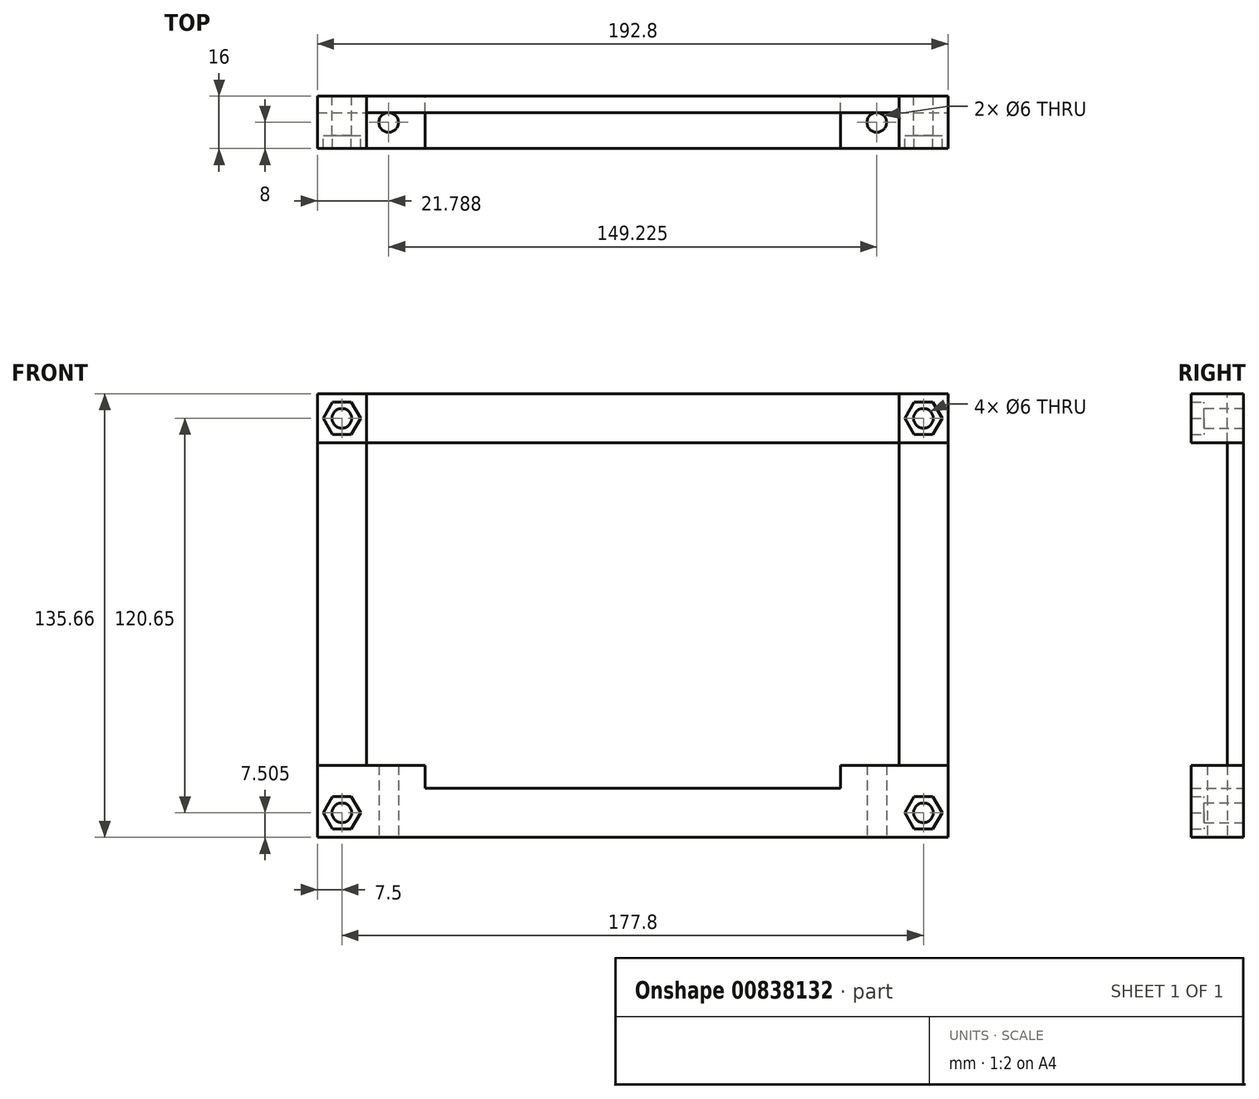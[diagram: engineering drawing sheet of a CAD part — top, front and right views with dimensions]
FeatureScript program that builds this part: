
annotation { "Feature Type Name" : "Feature", "Feature Type Description" : "" }
export const myFeature = defineFeature(function(context is Context, id is Id, definition is map)
    precondition{}
    {
        {
            var Q0;
            Q0=qCreatedBy(makeId("Front.planeOp"),FACE);
            var sketch = newSketch(context, id + "F0", { "sketchPlane" : qUnion([Q0])});
            skLineSegment(sketch, "E0.bottom", {"start": v(-88.9, 60.33) * mm, "end": v(88.9, 60.33) * mm, "construction": true});
            skLineSegment(sketch, "E0.top", {"start": v(-88.9, -60.32) * mm, "end": v(88.9, -60.32) * mm, "construction": true});
            skLineSegment(sketch, "E0.left", {"start": v(-88.9, 60.33) * mm, "end": v(-88.9, -60.32) * mm, "construction": true});
            skLineSegment(sketch, "E0.right", {"start": v(88.9, 60.33) * mm, "end": v(88.9, -60.32) * mm, "construction": true});
            skPoint(sketch, "E0.middle", {"position": v(0, 0) * mm});
            skCircle(sketch, "E1", {"center": v(-88.9, 60.33) * mm, "radius": 3 * mm});
            skCircle(sketch, "E2", {"center": v(88.9, 60.32) * mm, "radius": 3 * mm});
            skCircle(sketch, "E3", {"center": v(88.9, -60.32) * mm, "radius": 3 * mm});
            skCircle(sketch, "E4", {"center": v(-88.9, -60.32) * mm, "radius": 3 * mm});
            skLineSegment(sketch, "E5.bottom", {"start": v(-88.9, 60.33) * mm, "end": v(-96.4, 60.33) * mm, "construction": true});
            skLineSegment(sketch, "E5.top", {"start": v(-88.9, 67.83) * mm, "end": v(-96.4, 67.83) * mm, "construction": true});
            skLineSegment(sketch, "E5.left", {"start": v(-88.9, 60.33) * mm, "end": v(-88.9, 67.83) * mm, "construction": true});
            skLineSegment(sketch, "E5.right", {"start": v(-96.4, 60.33) * mm, "end": v(-96.4, 67.83) * mm, "construction": true});
            skLineSegment(sketch, "E6.bottom", {"start": v(88.9, -60.32) * mm, "end": v(96.4, -60.32) * mm, "construction": true});
            skLineSegment(sketch, "E6.top", {"start": v(88.9, -67.83) * mm, "end": v(96.4, -67.83) * mm, "construction": true});
            skLineSegment(sketch, "E6.left", {"start": v(88.9, -60.32) * mm, "end": v(88.9, -67.83) * mm, "construction": true});
            skLineSegment(sketch, "E6.right", {"start": v(96.4, -60.32) * mm, "end": v(96.4, -67.82) * mm, "construction": true});
            skLineSegment(sketch, "E7.bottom", {"start": v(-96.4, 67.83) * mm, "end": v(-81.4, 67.83) * mm});
            skLineSegment(sketch, "E7.top", {"start": v(-96.4, -67.83) * mm, "end": v(-81.4, -67.83) * mm});
            skLineSegment(sketch, "E7.left", {"start": v(-96.4, 67.83) * mm, "end": v(-96.4, -67.83) * mm});
            skLineSegment(sketch, "E7.right", {"start": v(-81.4, 67.82) * mm, "end": v(-81.4, -67.83) * mm});
            skLineSegment(sketch, "E8.bottom", {"start": v(96.4, -67.82) * mm, "end": v(-96.4, -67.83) * mm});
            skLineSegment(sketch, "E8.top", {"start": v(96.4, -52.83) * mm, "end": v(-96.4, -52.83) * mm});
            skLineSegment(sketch, "E8.left", {"start": v(96.4, -67.82) * mm, "end": v(96.4, -52.82) * mm});
            skLineSegment(sketch, "E8.right", {"start": v(-96.4, -67.83) * mm, "end": v(-96.4, -52.83) * mm});
            skLineSegment(sketch, "E9.bottom", {"start": v(96.4, -67.83) * mm, "end": v(81.4, -67.83) * mm});
            skLineSegment(sketch, "E9.top", {"start": v(96.4, 67.83) * mm, "end": v(81.4, 67.83) * mm});
            skLineSegment(sketch, "E9.left", {"start": v(96.4, -67.82) * mm, "end": v(96.4, 67.83) * mm});
            skLineSegment(sketch, "E9.right", {"start": v(81.4, -67.83) * mm, "end": v(81.4, 67.83) * mm});
            skLineSegment(sketch, "E10.bottom", {"start": v(-96.4, 67.83) * mm, "end": v(96.4, 67.83) * mm});
            skLineSegment(sketch, "E10.top", {"start": v(-96.4, 52.83) * mm, "end": v(96.4, 52.83) * mm});
            skLineSegment(sketch, "E10.left", {"start": v(-96.4, 67.83) * mm, "end": v(-96.4, 52.83) * mm});
            skLineSegment(sketch, "E10.right", {"start": v(96.4, 67.83) * mm, "end": v(96.4, 52.83) * mm});
            skLineSegment(sketch, "E11.bottom", {"start": v(0, -67.83) * mm, "end": v(-85.72, -67.83) * mm, "construction": true});
            skLineSegment(sketch, "E11.top", {"start": v(0, -71.83) * mm, "end": v(-85.72, -71.83) * mm, "construction": true});
            skLineSegment(sketch, "E11.left", {"start": v(0, -67.83) * mm, "end": v(0, -71.83) * mm, "construction": true});
            skLineSegment(sketch, "E11.right", {"start": v(-85.72, -67.83) * mm, "end": v(-85.72, -71.83) * mm, "construction": true});
            skLineSegment(sketch, "E12.bottom", {"start": v(0, -67.83) * mm, "end": v(85.73, -67.83) * mm, "construction": true});
            skLineSegment(sketch, "E12.top", {"start": v(0, -71.83) * mm, "end": v(85.73, -71.83) * mm, "construction": true});
            skLineSegment(sketch, "E12.right", {"start": v(85.73, -67.83) * mm, "end": v(85.73, -71.83) * mm, "construction": true});
            skLineSegment(sketch, "E13.bottom", {"start": v(-85.72, -71.83) * mm, "end": v(85.73, -71.83) * mm});
            skLineSegment(sketch, "E13.top", {"start": v(-85.72, -67.83) * mm, "end": v(85.73, -67.83) * mm});
            skLineSegment(sketch, "E13.left", {"start": v(-85.72, -71.83) * mm, "end": v(-85.72, -67.83) * mm});
            skLineSegment(sketch, "E13.right", {"start": v(85.73, -71.83) * mm, "end": v(85.73, -67.83) * mm});
            skLineSegment(sketch, "E14.bottom", {"start": v(85.73, -67.83) * mm, "end": v(70.73, -67.83) * mm});
            skLineSegment(sketch, "E14.left", {"start": v(85.73, -67.83) * mm, "end": v(85.73, -82.82) * mm});
            skLineSegment(sketch, "E15.bottom", {"start": v(-85.72, -67.83) * mm, "end": v(-63.5, -67.83) * mm});
            skLineSegment(sketch, "E15.top", {"start": v(-85.72, -71.83) * mm, "end": v(-63.5, -71.83) * mm});
            skLineSegment(sketch, "E15.left", {"start": v(-85.72, -67.83) * mm, "end": v(-85.72, -71.83) * mm});
            skLineSegment(sketch, "E15.right", {"start": v(-63.5, -67.83) * mm, "end": v(-63.5, -71.83) * mm});
            skLineSegment(sketch, "E16.bottom", {"start": v(85.73, -67.83) * mm, "end": v(63.5, -67.83) * mm});
            skLineSegment(sketch, "E16.top", {"start": v(85.73, -71.83) * mm, "end": v(63.5, -71.83) * mm});
            skLineSegment(sketch, "E16.left", {"start": v(85.73, -67.83) * mm, "end": v(85.73, -71.83) * mm});
            skLineSegment(sketch, "E16.right", {"start": v(63.5, -67.83) * mm, "end": v(63.5, -71.83) * mm});
            skCircle(sketch, "E17.cCircle", {"center": v(88.9, 60.32) * mm, "radius": 4.95 * mm, "construction": true});
            skLineSegment(sketch, "E17.0", {"start": v(91.76, 55.37) * mm, "end": v(86.04, 55.37) * mm});
            skLineSegment(sketch, "E17.1", {"start": v(86.04, 55.37) * mm, "end": v(83.18, 60.32) * mm});
            skLineSegment(sketch, "E17.2", {"start": v(83.18, 60.32) * mm, "end": v(86.04, 65.27) * mm});
            skLineSegment(sketch, "E17.3", {"start": v(86.04, 65.27) * mm, "end": v(91.76, 65.27) * mm});
            skLineSegment(sketch, "E17.4", {"start": v(91.76, 65.28) * mm, "end": v(94.62, 60.33) * mm});
            skLineSegment(sketch, "E17.5", {"start": v(94.62, 60.33) * mm, "end": v(91.76, 55.37) * mm});
            skPoint(sketch, "E17.0.midPoint", {"position": v(88.9, 55.38) * mm});
            skCircle(sketch, "E18.cCircle", {"center": v(88.9, -60.32) * mm, "radius": 4.95 * mm, "construction": true});
            skLineSegment(sketch, "E18.0", {"start": v(86.04, -55.37) * mm, "end": v(91.76, -55.37) * mm});
            skLineSegment(sketch, "E18.1", {"start": v(91.76, -55.37) * mm, "end": v(94.62, -60.33) * mm});
            skLineSegment(sketch, "E18.2", {"start": v(94.62, -60.33) * mm, "end": v(91.76, -65.28) * mm});
            skLineSegment(sketch, "E18.3", {"start": v(91.76, -65.28) * mm, "end": v(86.04, -65.28) * mm});
            skLineSegment(sketch, "E18.4", {"start": v(86.04, -65.28) * mm, "end": v(83.18, -60.32) * mm});
            skLineSegment(sketch, "E18.5", {"start": v(83.18, -60.32) * mm, "end": v(86.04, -55.37) * mm});
            skPoint(sketch, "E18.0.midPoint", {"position": v(88.9, -55.37) * mm});
            skCircle(sketch, "E19.cCircle", {"center": v(-88.9, -60.32) * mm, "radius": 4.95 * mm, "construction": true});
            skLineSegment(sketch, "E19.0", {"start": v(-91.76, -55.38) * mm, "end": v(-86.04, -55.38) * mm});
            skLineSegment(sketch, "E19.1", {"start": v(-86.04, -55.38) * mm, "end": v(-83.18, -60.33) * mm});
            skLineSegment(sketch, "E19.2", {"start": v(-83.18, -60.33) * mm, "end": v(-86.04, -65.27) * mm});
            skLineSegment(sketch, "E19.3", {"start": v(-86.04, -65.28) * mm, "end": v(-91.76, -65.28) * mm});
            skLineSegment(sketch, "E19.4", {"start": v(-91.76, -65.28) * mm, "end": v(-94.62, -60.33) * mm});
            skLineSegment(sketch, "E19.5", {"start": v(-94.62, -60.33) * mm, "end": v(-91.76, -55.38) * mm});
            skPoint(sketch, "E19.0.midPoint", {"position": v(-88.9, -55.38) * mm});
            skCircle(sketch, "E20.cCircle", {"center": v(-88.9, 60.33) * mm, "radius": 4.95 * mm, "construction": true});
            skLineSegment(sketch, "E20.0", {"start": v(-86.04, 55.38) * mm, "end": v(-91.76, 55.38) * mm});
            skLineSegment(sketch, "E20.1", {"start": v(-91.76, 55.38) * mm, "end": v(-94.62, 60.32) * mm});
            skLineSegment(sketch, "E20.2", {"start": v(-94.62, 60.32) * mm, "end": v(-91.76, 65.27) * mm});
            skLineSegment(sketch, "E20.3", {"start": v(-91.76, 65.28) * mm, "end": v(-86.04, 65.28) * mm});
            skLineSegment(sketch, "E20.4", {"start": v(-86.04, 65.28) * mm, "end": v(-83.18, 60.33) * mm});
            skLineSegment(sketch, "E20.5", {"start": v(-83.18, 60.33) * mm, "end": v(-86.04, 55.38) * mm});
            skPoint(sketch, "E20.0.midPoint", {"position": v(-88.9, 55.38) * mm});
            skLineSegment(sketch, "E21.bottom", {"start": v(-63.5, -52.83) * mm, "end": v(-96.4, -52.83) * mm});
            skLineSegment(sketch, "E21.top", {"start": v(-63.5, -45.83) * mm, "end": v(-96.4, -45.83) * mm});
            skLineSegment(sketch, "E21.left", {"start": v(-63.5, -52.83) * mm, "end": v(-63.5, -45.83) * mm});
            skLineSegment(sketch, "E21.right", {"start": v(-96.4, -52.83) * mm, "end": v(-96.4, -45.83) * mm});
            skLineSegment(sketch, "E22.bottom", {"start": v(63.5, -52.83) * mm, "end": v(96.4, -52.83) * mm});
            skLineSegment(sketch, "E22.top", {"start": v(63.5, -45.83) * mm, "end": v(96.4, -45.83) * mm});
            skLineSegment(sketch, "E22.left", {"start": v(63.5, -52.83) * mm, "end": v(63.5, -45.83) * mm});
            skLineSegment(sketch, "E22.right", {"start": v(96.4, -52.82) * mm, "end": v(96.4, -45.83) * mm});
            skSolve(sketch);
        }
        {
            var Q0;
            {var subQ0=sQuery(id+"F0.wireOp",EDGE,"E8.bottom");var subQ7=makeQuery(id+"F0.imprint","IMPRINT",VERTEX,{"derivedFrom":subQ0});Q0=makeQuery(id+"F0.imprint","IMPRINT",FACE,{"disambiguationData":[TD([[makeQuery(id+"F0.imprint","IMPRINT",EDGE,{"disambiguationData":[TD([[subQ7,1.0]])],"derivedFrom":subQ0}),-1.0]])]});}
            var Q1;
            Q1=makeQuery(id+"F0.imprint","IMPRINT",FACE,{"disambiguationData":[TD([[makeQuery(id+"F0.imprint","IMPRINT",EDGE,{"derivedFrom":sQuery(id+"F0.wireOp",EDGE,"E19.0")}),1.0]])]});
            var Q2;
            {var subQ5=sQuery(id+"F0.wireOp",EDGE,"E8.left");Q2=makeQuery(id+"F0.imprint","IMPRINT",FACE,{"disambiguationData":[TD([[makeQuery(id+"F0.imprint","IMPRINT",EDGE,{"derivedFrom":subQ5}),1.0]])]});}
            var Q3;
            {var subQ5=sQuery(id+"F0.wireOp",EDGE,"E7.bottom");Q3=makeQuery(id+"F0.imprint","IMPRINT",FACE,{"disambiguationData":[TD([[makeQuery(id+"F0.imprint","IMPRINT",EDGE,{"derivedFrom":subQ5}),-1.0]])]});}
            var Q4;
            {var subQ1=sQuery(id+"F0.wireOp",EDGE,"E9.top");Q4=makeQuery(id+"F0.imprint","IMPRINT",FACE,{"disambiguationData":[TD([[makeQuery(id+"F0.imprint","IMPRINT",EDGE,{"derivedFrom":subQ1}),1.0]])]});}
            var Q5;
            {var subQ0=sQuery(id+"F0.wireOp",EDGE,"E8.top");var subQ1=sQuery(id+"F0.wireOp",EDGE,"E7.left");var subQ2=makeQuery(id+"F0.imprint","INTERSECT",VERTEX,{"derivedFrom":[subQ1,subQ0]});var subQ9=sQuery(id+"F0.wireOp",EDGE,"E21.left");Q5=qUnion([makeQuery(id+"F0.imprint","IMPRINT",FACE,{"disambiguationData":[TD([[makeQuery(id+"F0.imprint","IMPRINT",EDGE,{"derivedFrom":subQ9}),1.0]])]}),makeQuery(id+"F0.imprint","IMPRINT",FACE,{"disambiguationData":[TD([[makeQuery(id+"F0.imprint","IMPRINT",EDGE,{"disambiguationData":[TD([[subQ2,1.0]])],"derivedFrom":subQ1}),1.0]])]})]);}
            var Q6;
            {var subQ0=sQuery(id+"F0.wireOp",EDGE,"E22.left");var subQ2=sQuery(id+"F0.wireOp",EDGE,"E9.right");var subQ4=sQuery(id+"F0.wireOp",EDGE,"E22.top");var subQ5=makeQuery(id+"F0.imprint","INTERSECT",VERTEX,{"derivedFrom":[subQ2,subQ4]});var subQ6=makeQuery(id+"F0.imprint","IMPRINT",EDGE,{"disambiguationData":[TD([[subQ5,1.0]])],"derivedFrom":subQ2});Q6=qUnion([makeQuery(id+"F0.imprint","IMPRINT",FACE,{"disambiguationData":[TD([[subQ6,-1.0]])]}),makeQuery(id+"F0.imprint","IMPRINT",FACE,{"disambiguationData":[TD([[makeQuery(id+"F0.imprint","IMPRINT",EDGE,{"derivedFrom":subQ0}),-1.0]])]})]);}
            extrude(context, id + "F1", {"entities" : qUnion([Q0, Q1, Q2, Q3, Q4, Q5, Q6]), "depth" : 16 * mm, "offsetDistance" : 25 * mm});
        }
        {
            var Q0;
            Q0=makeQuery(id+"F0.imprint","IMPRINT",FACE,{"disambiguationData":[TD([[makeQuery(id+"F0.imprint","IMPRINT",EDGE,{"derivedFrom":sQuery(id+"F0.wireOp",EDGE,"E4")}),-1.0]])]});
            var Q1;
            Q1=makeQuery(id+"F0.imprint","IMPRINT",FACE,{"disambiguationData":[TD([[makeQuery(id+"F0.imprint","IMPRINT",EDGE,{"derivedFrom":sQuery(id+"F0.wireOp",EDGE,"E3")}),-1.0]])]});
            var Q2;
            Q2=makeQuery(id+"F0.imprint","IMPRINT",FACE,{"disambiguationData":[TD([[makeQuery(id+"F0.imprint","IMPRINT",EDGE,{"derivedFrom":sQuery(id+"F0.wireOp",EDGE,"E1")}),-1.0]])]});
            var Q3;
            Q3=makeQuery(id+"F0.imprint","IMPRINT",FACE,{"disambiguationData":[TD([[makeQuery(id+"F0.imprint","IMPRINT",EDGE,{"derivedFrom":sQuery(id+"F0.wireOp",EDGE,"E2")}),-1.0]])]});
            extrude(context, id + "F2", {"entities" : qUnion([Q0, Q1, Q2, Q3]), "operationType" : NewBodyOperationType.ADD, "depth" : 12 * mm, "offsetDistance" : 25 * mm});
        }
        {
            var Q0;
            {var subQ0=sQuery(id+"F0.wireOp",EDGE,"E10.top");var subQ1=sQuery(id+"F0.wireOp",EDGE,"E7.left");var subQ2=makeQuery(id+"F0.imprint","INTERSECT",VERTEX,{"derivedFrom":[subQ1,subQ0]});Q0=makeQuery(id+"F0.imprint","IMPRINT",FACE,{"disambiguationData":[TD([[makeQuery(id+"F0.imprint","IMPRINT",EDGE,{"disambiguationData":[TD([[subQ2,-1.0]])],"derivedFrom":subQ1}),1.0]])]});}
            var Q1;
            {var subQ0=sQuery(id+"F0.wireOp",EDGE,"E10.bottom");Q1=makeQuery(id+"F0.imprint","IMPRINT",FACE,{"disambiguationData":[TD([[makeQuery(id+"F0.imprint","IMPRINT",EDGE,{"derivedFrom":subQ0}),-1.0]])]});}
            var Q2;
            {var subQ0=sQuery(id+"F0.wireOp",EDGE,"E22.top");var subQ1=sQuery(id+"F0.wireOp",EDGE,"E9.left");var subQ2=makeQuery(id+"F0.imprint","INTERSECT",VERTEX,{"derivedFrom":[subQ1,subQ0]});Q2=makeQuery(id+"F0.imprint","IMPRINT",FACE,{"disambiguationData":[TD([[makeQuery(id+"F0.imprint","IMPRINT",EDGE,{"disambiguationData":[TD([[subQ2,-1.0]])],"derivedFrom":subQ1}),1.0]])]});}
            extrude(context, id + "F3", {"entities" : qUnion([Q0, Q1, Q2]), "depth" : 5 * mm, "offsetDistance" : 25 * mm});
        }
        {
            var Q0;
            Q0=makeQuery(id+"F1.opExtrude","SWEPT_FACE",FACE,{"disambiguationData":[OSD([sQuery(id+"F0.wireOp",EDGE,"E7.top"),sQuery(id+"F0.wireOp",EDGE,"E8.bottom")])]});
            cPlane(context, id + "F4", {"entities" : qUnion([Q0]), "cplaneType" : CPlaneType.OFFSET, "offset" : 0 * mm, "width" : 150 * mm, "height" : 150 * mm});
        }
        {
            var Q0;
            Q0=qCreatedBy(id+"F4.planeOp",FACE);
            var sketch = newSketch(context, id + "F5", { "sketchPlane" : qUnion([Q0])});
            skLineSegment(sketch, "E23.bottom", {"start": v(-85.72, 0) * mm, "end": v(-63.5, 0) * mm, "construction": true});
            skLineSegment(sketch, "E23.top", {"start": v(-85.72, 16) * mm, "end": v(-63.5, 16) * mm, "construction": true});
            skLineSegment(sketch, "E23.left", {"start": v(-85.72, 0) * mm, "end": v(-85.72, 16) * mm, "construction": true});
            skLineSegment(sketch, "E23.right", {"start": v(-63.5, 0) * mm, "end": v(-63.5, 16) * mm, "construction": true});
            skPoint(sketch, "E24", {"position": v(-74.61, 8) * mm});
            skPoint(sketch, "E24.positionSnap0", {"position": v(-85.72, 8) * mm});
            skPoint(sketch, "E24.positionSnap1", {"position": v(-74.61, 0) * mm});
            skLineSegment(sketch, "E25.bottom", {"start": v(63.5, 16) * mm, "end": v(85.73, 16) * mm, "construction": true});
            skLineSegment(sketch, "E25.top", {"start": v(63.5, 0) * mm, "end": v(85.73, 0) * mm, "construction": true});
            skLineSegment(sketch, "E25.left", {"start": v(63.5, 16) * mm, "end": v(63.5, 0) * mm, "construction": true});
            skLineSegment(sketch, "E25.right", {"start": v(85.73, 16) * mm, "end": v(85.73, 0) * mm, "construction": true});
            skPoint(sketch, "E26", {"position": v(74.61, 8) * mm});
            skPoint(sketch, "E26.positionSnap0", {"position": v(63.5, 8) * mm});
            skPoint(sketch, "E26.positionSnap1", {"position": v(74.61, 0) * mm});
            skSolve(sketch);
        }
        {
            var Q0;
            Q0=sQuery(id+"F5.wireOp",VERTEX,"E26");
            var Q1;
            Q1=sQuery(id+"F5.wireOp",VERTEX,"E24");
            var Q2;
            Q2=makeQuery(id+"F1.opExtrude","SWEPT_BODY",BODY,{"disambiguationData":[OSD([sQuery(id+"F0.wireOp",EDGE,"E7.top"),sQuery(id+"F0.wireOp",EDGE,"E7.left"),sQuery(id+"F0.wireOp",EDGE,"E8.bottom"),sQuery(id+"F0.wireOp",EDGE,"E8.top"),sQuery(id+"F0.wireOp",EDGE,"E8.left"),sQuery(id+"F0.wireOp",EDGE,"E9.left"),sQuery(id+"F0.wireOp",EDGE,"E18.0"),sQuery(id+"F0.wireOp",EDGE,"E18.1"),sQuery(id+"F0.wireOp",EDGE,"E18.2"),sQuery(id+"F0.wireOp",EDGE,"E18.3"),sQuery(id+"F0.wireOp",EDGE,"E18.4"),sQuery(id+"F0.wireOp",EDGE,"E18.5"),sQuery(id+"F0.wireOp",EDGE,"E19.0"),sQuery(id+"F0.wireOp",EDGE,"E19.1"),sQuery(id+"F0.wireOp",EDGE,"E19.2"),sQuery(id+"F0.wireOp",EDGE,"E19.3"),sQuery(id+"F0.wireOp",EDGE,"E19.4"),sQuery(id+"F0.wireOp",EDGE,"E19.5"),sQuery(id+"F0.wireOp",EDGE,"E21.top"),sQuery(id+"F0.wireOp",EDGE,"E21.left"),sQuery(id+"F0.wireOp",EDGE,"E22.top"),sQuery(id+"F0.wireOp",EDGE,"E22.left")])]});
            hole(context, id + "F6", {"style" : HoleStyle.SIMPLE, "endStyle" : HoleEndStyle.THROUGH, "holeDiameter" : 6 * mm, "majorDiameter" : 5 * mm, "isTappedThrough" : true, "tappedDepth" : 12 * mm, "tapClearance" : 3, "locations" : qUnion([Q0, Q1]), "scope" : qUnion([Q2])});
        }
    });
